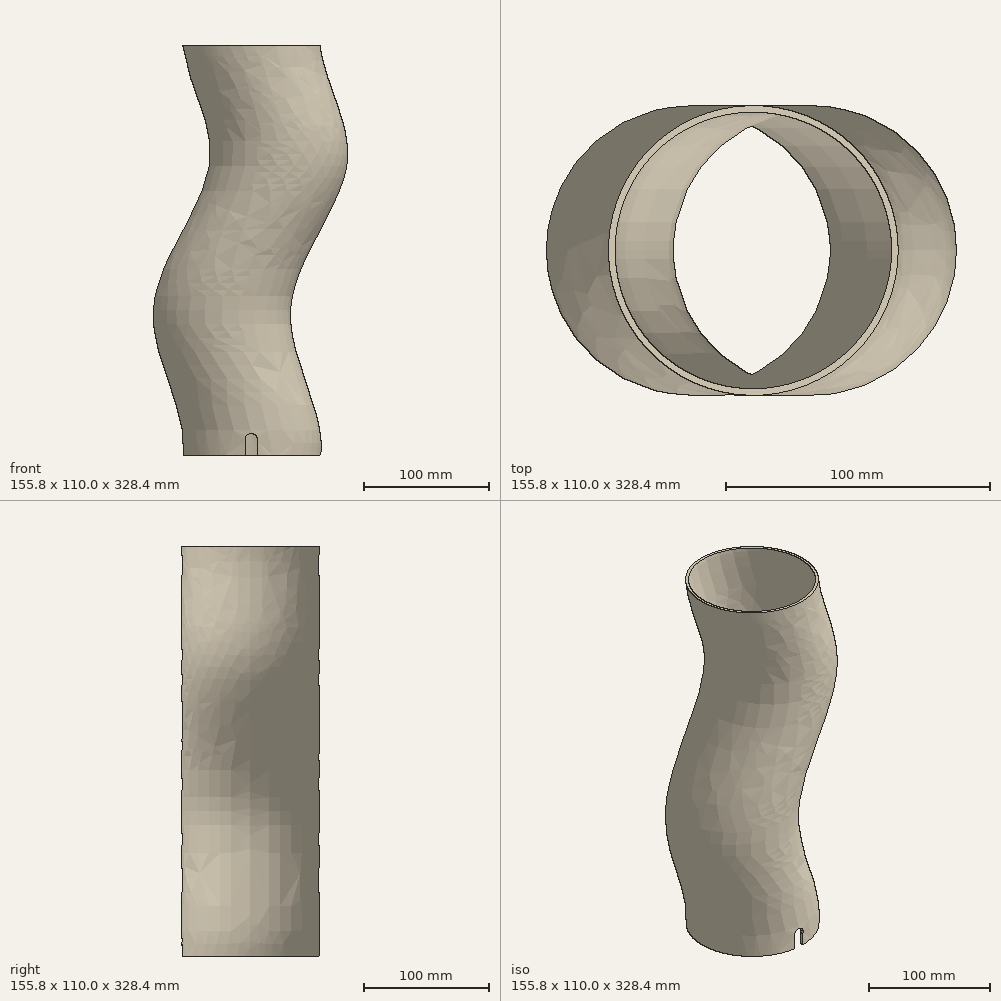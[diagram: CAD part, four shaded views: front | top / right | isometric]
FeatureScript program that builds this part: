
annotation { "Feature Type Name" : "Feature", "Feature Type Description" : "" }
export const myFeature = defineFeature(function(context is Context, id is Id, definition is map)
    precondition{}
    {
        {
            var Q0;
            Q0=qCreatedBy(makeId("Top.planeOp"),FACE);
            var sketch = newSketch(context, id + "F0", { "sketchPlane" : qUnion([Q0])});
            skCircle(sketch, "E0", {"center": v(0, 0) * mm, "radius": 55 * mm});
            skSolve(sketch);
        }
        {
            var Q0;
            Q0=qCreatedBy(makeId("Front.planeOp"),FACE);
            var sketch = newSketch(context, id + "F1", { "sketchPlane" : qUnion([Q0])});
            skFitSpline(sketch, "E1", {"points": [v(0, 0) * mm, v(-23.51, 120.1) * mm, v(21.6, 237.32) * mm, v(0, 332.37) * mm], "startDerivative": vector(60.56, 319.02) * mm, "endDerivative": vector(-39.36, 316.16) * mm});
            skSolve(sketch);
        }
        {
            var Q0;
            Q0=makeQuery(id+"F0.imprint","IMPRINT",FACE,{"disambiguationData":[TD([[makeQuery(id+"F0.imprint","IMPRINT",EDGE,{"derivedFrom":sQuery(id+"F0.wireOp",EDGE,"E0")}),1.0]])]});
            var Q1;
            Q1=sQuery(id+"F1.wireOp",EDGE,"E1");
            sweep(context, id + "F2", {"profiles" : qUnion([Q0]), "path" : qUnion([Q1]), "keepProfileOrientation" : true});
        }
        {
            var Q0;
            Q0=makeQuery(id+"F2.opSweep","CAP_FACE",FACE,{"disambiguationData":[OSD([sQuery(id+"F0.wireOp",EDGE,"E0"),sQuery(id+"F1.wireOp",VERTEX,"E1.end")])],"isStart":false});
            shell(context, id + "F3", {"entities" : qUnion([Q0]), "thickness" : 2.5 * mm});
        }
        {
            var Q0;
            Q0=qCreatedBy(makeId("Top.planeOp"),FACE);
            var sketch = newSketch(context, id + "F4", { "sketchPlane" : qUnion([Q0])});
            skCircle(sketch, "E2", {"center": v(149.06, 28.61) * mm, "radius": 76.55 * mm});
            skSolve(sketch);
        }
        {
            var Q0;
            Q0 = qSketchRegion(id + "F4", true);
            extrude(context, id + "F5", {"entities" : qUnion([Q0]), "depth" : 25 * mm, "offsetDistance" : 25 * mm});
        }
        {
            var Q0;
            Q0=makeQuery(id+"F5.opExtrude","SWEPT_BODY",BODY,{"disambiguationData":[OSD([sQuery(id+"F4.wireOp",EDGE,"E2")])]});
            transform(context, id + "F6", {"entities" : qUnion([Q0]), "transformType" : TransformType.TRANSLATION_3D, "dx" : -147 * mm, "dy" : -29 * mm, "dz" : -21 * mm, "makeCopy" : false});
        }
        {
            var Q0;
            Q0=makeQuery(id+"F5.opExtrude","SWEPT_BODY",BODY,{"disambiguationData":[OSD([sQuery(id+"F4.wireOp",EDGE,"E2")])]});
            var Q1;
            Q1=makeQuery(id+"F2.opSweep","SWEPT_BODY",BODY,{"disambiguationData":[OSD([sQuery(id+"F0.wireOp",EDGE,"E0"),sQuery(id+"F1.wireOp",EDGE,"E1")])]});
            booleanBodies(context, id + "F7", {"operationType" : BooleanOperationType.SUBTRACTION, "tools" : qUnion([Q0]), "targets" : qUnion([Q1])});
        }
        {
            var Q0;
            Q0=qCreatedBy(makeId("Front.planeOp"),FACE);
            var sketch = newSketch(context, id + "F8", { "sketchPlane" : qUnion([Q0])});
            skCircle(sketch, "E3", {"center": v(-154.24, 65.01) * mm, "radius": 5 * mm});
            skSolve(sketch);
        }
        {
            var Q0;
            Q0 = qSketchRegion(id + "F8", true);
            extrude(context, id + "F9", {"entities" : qUnion([Q0]), "depth" : 25 * mm, "offsetDistance" : 25 * mm});
        }
        {
            var Q0;
            Q0=makeQuery(id+"F9.opExtrude","SWEPT_BODY",BODY,{"disambiguationData":[OSD([sQuery(id+"F8.wireOp",EDGE,"E3")])]});
            transform(context, id + "F10", {"entities" : qUnion([Q0]), "transformType" : TransformType.TRANSLATION_3D, "dx" : 154.2 * mm, "dy" : -40.4 * mm, "dz" : -48.6 * mm, "makeCopy" : false});
        }
        {
            var Q0;
            Q0=makeQuery(id+"F9.opExtrude","SWEPT_BODY",BODY,{"disambiguationData":[OSD([sQuery(id+"F8.wireOp",EDGE,"E3")])]});
            var Q1;
            Q1=makeQuery(id+"F2.opSweep","SWEPT_BODY",BODY,{"disambiguationData":[OSD([sQuery(id+"F0.wireOp",EDGE,"E0"),sQuery(id+"F1.wireOp",EDGE,"E1")])]});
            booleanBodies(context, id + "F11", {"operationType" : BooleanOperationType.SUBTRACTION, "tools" : qUnion([Q0]), "targets" : qUnion([Q1])});
        }
        {
            var Q0;
            Q0=qCreatedBy(makeId("Front.planeOp"),FACE);
            var sketch = newSketch(context, id + "F12", { "sketchPlane" : qUnion([Q0])});
            skLineSegment(sketch, "E4.bottom", {"start": v(-9.44, 9.3) * mm, "end": v(0, 9.3) * mm});
            skLineSegment(sketch, "E4.top", {"start": v(-9.44, -5.3) * mm, "end": v(0, -5.3) * mm});
            skLineSegment(sketch, "E4.left", {"start": v(-9.44, 9.3) * mm, "end": v(-9.44, -5.3) * mm});
            skLineSegment(sketch, "E4.right", {"start": v(0, 9.3) * mm, "end": v(0, -5.3) * mm});
            skSolve(sketch);
        }
        {
            var Q0;
            Q0 = qSketchRegion(id + "F12", true);
            extrude(context, id + "F13", {"entities" : qUnion([Q0]), "endBound" : BoundingType.SYMMETRIC, "depth" : 20 * mm, "offsetDistance" : 25 * mm});
        }
        {
            var Q0;
            Q0=makeQuery(id+"F13.opExtrude","SWEPT_BODY",BODY,{"disambiguationData":[OSD([sQuery(id+"F12.wireOp",EDGE,"E4.bottom"),sQuery(id+"F12.wireOp",EDGE,"E4.top"),sQuery(id+"F12.wireOp",EDGE,"E4.left"),sQuery(id+"F12.wireOp",EDGE,"E4.right")])]});
            transform(context, id + "F14", {"entities" : qUnion([Q0]), "transformType" : TransformType.TRANSLATION_3D, "dx" : 4.7 * mm, "dy" : -47.6 * mm, "dz" : 6.6 * mm, "makeCopy" : false});
        }
        {
            var Q0;
            Q0=makeQuery(id+"F13.opExtrude","SWEPT_BODY",BODY,{"disambiguationData":[OSD([sQuery(id+"F12.wireOp",EDGE,"E4.bottom"),sQuery(id+"F12.wireOp",EDGE,"E4.top"),sQuery(id+"F12.wireOp",EDGE,"E4.left"),sQuery(id+"F12.wireOp",EDGE,"E4.right")])]});
            var Q1;
            Q1=makeQuery(id+"F2.opSweep","SWEPT_BODY",BODY,{"disambiguationData":[OSD([sQuery(id+"F0.wireOp",EDGE,"E0"),sQuery(id+"F1.wireOp",EDGE,"E1")])]});
            booleanBodies(context, id + "F15", {"operationType" : BooleanOperationType.SUBTRACTION, "tools" : qUnion([Q0]), "targets" : qUnion([Q1])});
        }
    });
